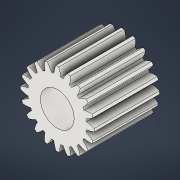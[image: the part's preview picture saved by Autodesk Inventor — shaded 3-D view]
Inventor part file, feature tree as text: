
AUTODESK INVENTOR PART (.ipt)
format: ipt  version: 2021 (Build 250183000, 183)  size: 282,624 bytes
history: native  units: mm (DEFAULTED — no unit token found)
features: plane x3, other x3, sketch x3, extrude x2
ambient origin geometry x8: Origin, YZ Plane, XZ Plane, XY Plane, X Axis, Y Axis, Z Axis, Center Point
bodies: Solid1 (feature_tree)
feature tree (11):
  extrude  "Extrusion1"  Depth=1.75mm TaperAngle=0.0deg
  plane  "Work Plane2"
  plane  "Work Plane8"
  plane  "Work Plane9"
  other  "Engrenagem reta"
  extrude  "Extrusão2"  Depth=10.0mm TaperAngle=0.0deg
  sketch  "Sketch1"  dims[d0=1.979988mm d1=1.75mm d2=0.0mm]
  sketch  "Sketch2"  dims[d3=1.8mm d4=10.0mm d5=0.0mm]
  other  "Srf1"
  sketch  "Esboço3"  dims[d16=3.597588mm d17=0.0mm d34=1.570796mm d39=0.0mm d41=0.0mm d43=3.597588mm d46=3.597588mm d47=0.0mm d48=0.0mm d49=0.9mm d50=1.75mm d51=0.0mm]
  other  "Diâmetro do flanco"
